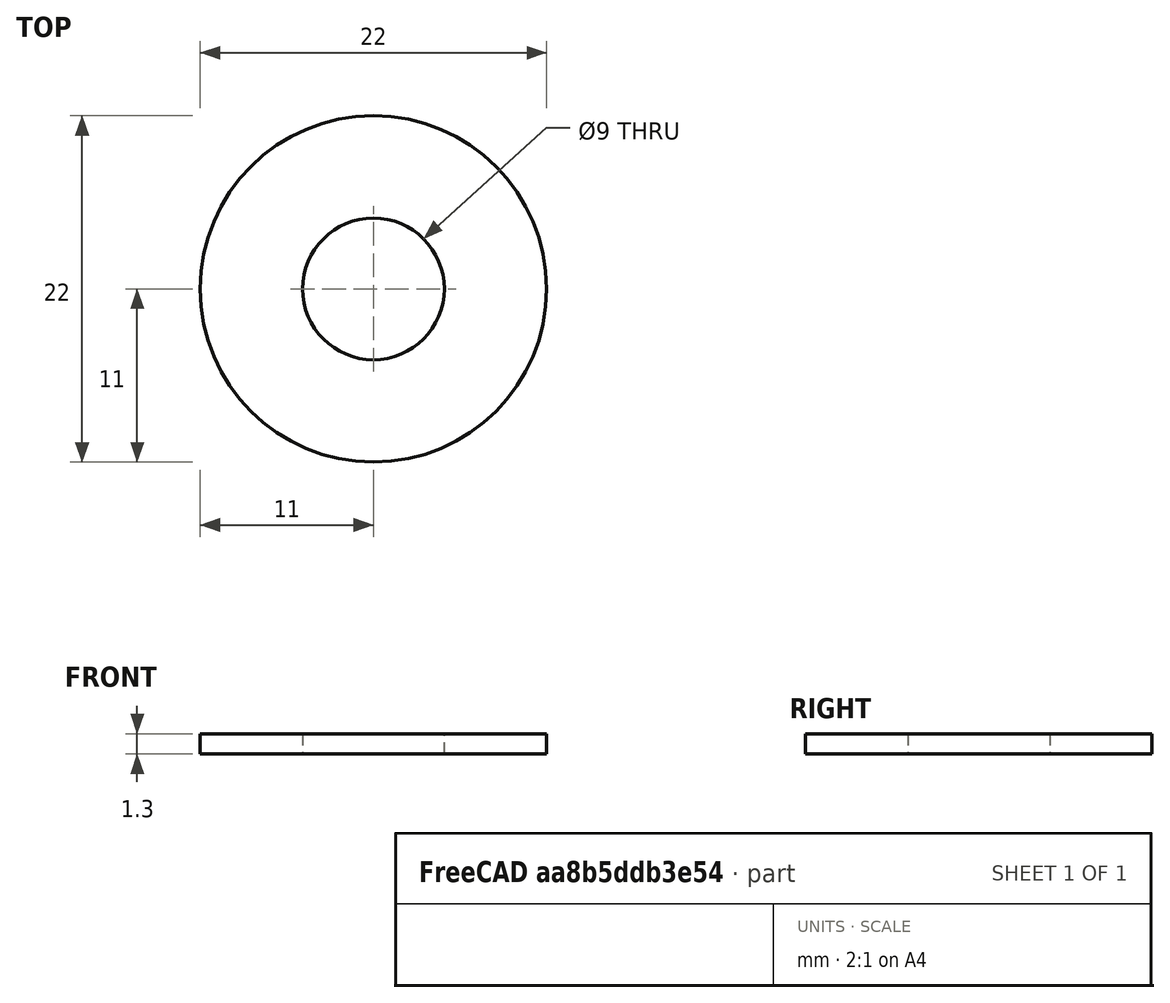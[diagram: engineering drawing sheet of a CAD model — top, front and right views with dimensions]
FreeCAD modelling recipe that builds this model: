
FCSTD DOCUMENT  (FreeCAD 0.19R24276 (Git))
Label: Shaiba_d9_d22_h_1_3
License: All rights reserved
LicenseURL: http://en.wikipedia.org/wiki/All_rights_reserved
objects: Sketcher::SketchObject×1, PartDesign::Pad×1, PartDesign::Body×1
note: 4 computed .brp shape members not serialized (recipe doc carries the construction recipe); baked Part::Feature solids carry a one-line shape summary decoded from their .brp

FEATURE [Sketcher::SketchObject] Sketch
  FullyConstrained = true
  MapMode = 5
  Support = -> [XY_Plane]
  sketch-geometry (2):
    g0: Circle CenterX=0 CenterY=0 CenterZ=0 NormalX=0 NormalY=0 NormalZ=1 AngleXU=0 Radius=4.5
    g1: Circle CenterX=0 CenterY=0 CenterZ=0 NormalX=0 NormalY=0 NormalZ=1 AngleXU=0 Radius=11
  constraints (4):
    c: Coincident(g0,g-1)
    c: Coincident(g1,g0)
    c: Diameter(g0) = 9
    c: Diameter(g1) = 22
FEATURE [PartDesign::Pad] Pad
  Direction = (1,1,1)
  Length = 1.3
  Length2 = 100
  Profile = -> Sketch
  Type = 0
FEATURE [PartDesign::Body] Body
  Group = -> [Sketch,Pad]
  Origin = -> Origin
  Tip = -> Pad
